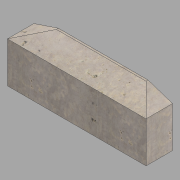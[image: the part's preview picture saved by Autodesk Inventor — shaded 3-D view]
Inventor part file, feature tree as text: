
AUTODESK INVENTOR PART (.ipt)
format: ipt  version: 2022.1 (Build 261234020, 234B)  size: 145,408 bytes
history: native  units: in
note: dims shown in document units (in); Inventor stores cm internally (conversion verified against a paired STEP export)
features: extrude x4, sketch x3
ambient origin geometry x8: Origin, YZ Plane, XZ Plane, XY Plane, X Axis, Y Axis, Z Axis, Center Point
bodies: Solid1 (feature_tree)
feature tree (7):
  extrude  "Extrusion1"  Depth=6.5in
  extrude  "Extrusion2"  Depth=12.0in
  sketch  "Sketch3"  dims[d5=2.0in d6=0.0in d7=0.0in d8=6.0in d9=2.0in d10=0.0in d11=0.0in d12=0.0in d13=0.0in]
  extrude  "Extrusion3"  TaperAngle=0.0deg  [1 undecoded]
  extrude  "Extrusion4"  Depth=6.0in
  sketch  "Sketch1"  dims[d0=34.0in d1=6.5in]
  sketch  "Sketch2"  dims[d2=12.0in d3=0.0in d4=0.5in]
note: 1 required parameter value undecoded (feature->parameter linkage not recoverable at this tier; creation-order binding heuristic only, values carry confidence <= 0.55)
